# Revit family: T100022
name_source: partatom
category: Furniture
units: mm (PartAtom-declared; Revit-internal decimal feet)

## family parameters
Always vertical = Yes
Cut with Voids When Loaded = No
OmniClass Number = 23.40.20.00
OmniClass Title = General Furniture and Specialties
Render Appearance Source = Family Geometry
Room Calculation Point = No
Shared = No
Work Plane-Based = No

## types (1)
- T100022
    Assembly Code = E2020200
    Back Coverage Material = OFS BRANDS IMPULSE Back Coverage Plastic
    Catalog = http://ofsbrands.com
    Chassis Material = OFS BRANDS IMPULSE Chassis Wood
    Conector Material = OFS BRANDS IMPULSE Conector Metal
    Default Elevation = 0"
    Depth = 100"
    Description = OFS BRANDS OFS IMPULSE G2 TYPICAL T100022
    Drawer Front Material = OFS BRANDS IMPULSE Drawer Front Wood
    Grommet  Material = OFS BRANDS IMPULSE Grommet Metal
    Height = 71 15/16"
    Lock Material = OFS BRANDS IMPULSE Lock Metal
    Manufacturer = OFS
    Model = T100022
    Pull Material = OFS BRANDS IMPULSE Pull Metal
    Tackboard Material = OFS BRANDS IMPULSE Tackboard Fabric
    Tool Rail Material = OFS BRANDS IMPULSE Tool Rail Metal
    Top Core Material = OFS BRANDS IMPULSE Top Core Wood
    URL = http://www.ofsbrands.com
    Width = 135 9/16"

## geometry (parser evidence)
native form markers: Blend x8, Sweep x8
no freeform markers — native parametric forms only
